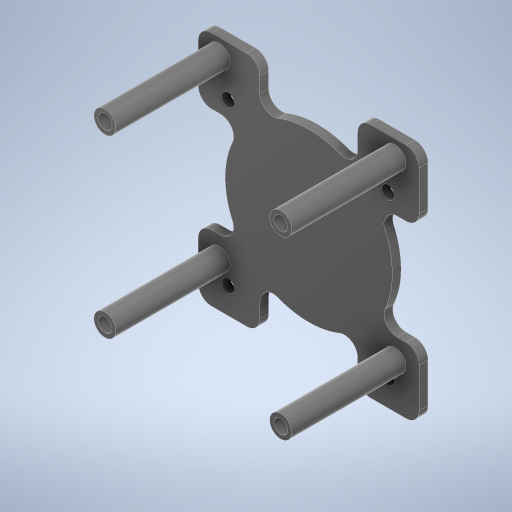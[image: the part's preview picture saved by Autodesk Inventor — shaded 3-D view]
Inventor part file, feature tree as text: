
AUTODESK INVENTOR PART (.ipt)
format: ipt  version: 2023.1 (Build 271208000, 208)  size: 369,152 bytes
history: native  units: in
note: dims shown in document units (in); Inventor stores cm internally (conversion verified against a paired STEP export)
features: reference x13, other x6, fillet x3, extrude x2, sketch x2, plane x1
ambient origin geometry x8: Origin, YZ Plane, XZ Plane, XY Plane, X Axis, Y Axis, Z Axis, Center Point
bodies: Solid1 (feature_tree)
feature tree (27):
  plane  "Work Plane1"
  extrude  "Extrusion1"  Depth=1.9783in
  fillet  "Fillet1"  Radius=2.1181in
  fillet  "Fillet2"  Radius=1.0591in
  extrude  "Extrusion2"  Depth=0.1181in
  fillet  "Fillet3"  Radius=0.1181in
  sketch  "Sketch1"  dims[d0=0.0787in d1=0.0in d10=1.9783in d11=2.1181in d12=0.9892in d13=1.0591in]
  reference  "Reference1"
  reference  "Reference2"
  reference  "Reference3"
  reference  "Reference4"
  reference  "Reference5"
  reference  "Reference6"
  reference  "Reference7"
  reference  "Reference8"
  reference  "Reference9"
  sketch  "Sketch2"  dims[d14=1.4961in d15=0.1181in d16=0.1181in d17=0.1969in d18=0.1969in d19=0.1969in d20=0.1969in d21=1.0236in d22=0.0in d23=0.1181in]
  reference  "Reference10"
  reference  "Reference11"
  reference  "Reference12"
  reference  "Reference13"
  other  "Assembly2"
  other  "Assembly - Fixed:1"
  other  "BaseParal:1"
  other  "BTS7960 43A HIGH POWER H BRIDGE MODULE:1"
  other  "PCB, BTS7960 43A HIGH POWER H BRIDGE MODULE_1"
  other  "HEATSINK, BTS7960 43A HIGH POWER H BRIDGE MODULE_2"
